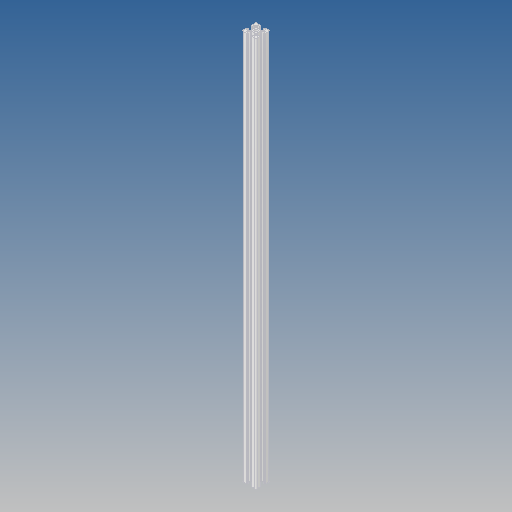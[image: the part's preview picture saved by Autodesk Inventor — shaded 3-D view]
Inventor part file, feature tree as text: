
AUTODESK INVENTOR PART (.ipt)
format: ipt  version: 2018 (Build 220112000, 112)  size: 246,784 bytes
history: native  units: mm
features: other x1, extrude x1, sketch x1, projected_geometry x1
ambient origin geometry x8: Origin, YZ Plane, XZ Plane, XY Plane, X Axis, Y Axis, Z Axis, Center Point
bodies: Solid1 (feature_tree), Body1 (feature_tree)
feature tree (4):
  other  "<userpath>\OneDrive\Objet3D\3DPrinter\Parameters.xlsx"
  extrude  "Extrusion1"  [1 undecoded]
  sketch  "Sketch1"  dims[d0=460.0mm d1=0.0mm]
  projected_geometry  "Projected Loop1"
note: 1 required parameter value undecoded (feature->parameter linkage not recoverable at this tier; creation-order binding heuristic only, values carry confidence <= 0.55)
